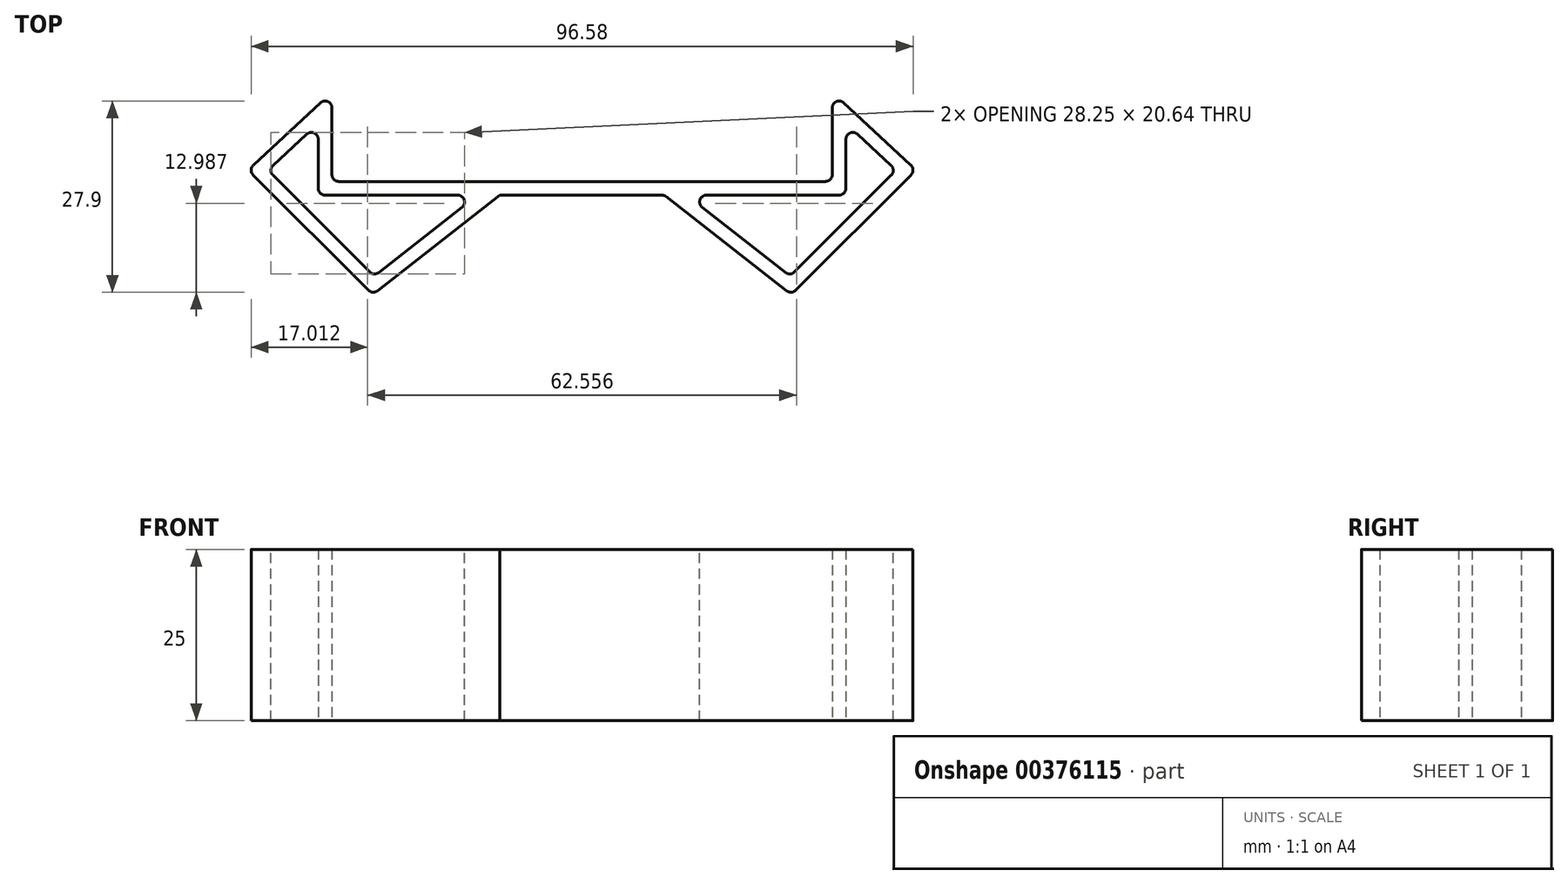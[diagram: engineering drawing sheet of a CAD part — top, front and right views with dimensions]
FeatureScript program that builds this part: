
annotation { "Feature Type Name" : "Feature", "Feature Type Description" : "" }
export const myFeature = defineFeature(function(context is Context, id is Id, definition is map)
    precondition{}
    {
        {
            var Q0;
            Q0=qCreatedBy(makeId("Top.planeOp"),FACE);
            var sketch = newSketch(context, id + "F0", { "sketchPlane" : qUnion([Q0])});
            skLineSegment(sketch, "E0", {"start": v(0, 0) * mm, "end": v(-36.5, 0) * mm});
            skLineSegment(sketch, "E1", {"start": v(-36.5, 0) * mm, "end": v(-36.5, 13.03) * mm});
            skLineSegment(sketch, "E2", {"start": v(-30.55, -16.5) * mm, "end": v(-12, -2) * mm});
            skLineSegment(sketch, "E3", {"start": v(-12, -2) * mm, "end": v(0, -2) * mm});
            skLineSegment(sketch, "E4", {"start": v(0, 14.81) * mm, "end": v(0, -16.78) * mm});
            skLineSegment(sketch, "E5.0", {"start": v(-38.5, -2) * mm, "end": v(-38.5, 15.49) * mm});
            skLineSegment(sketch, "E5.1", {"start": v(0, -2) * mm, "end": v(-38.5, -2) * mm});
            skLineSegment(sketch, "E6.0", {"start": v(-30.39, -13.83) * mm, "end": v(-15.25, -2) * mm});
            skLineSegment(sketch, "E7", {"start": v(-30.55, -16.5) * mm, "end": v(-48.73, 1.69) * mm});
            skLineSegment(sketch, "E8", {"start": v(-48.73, 1.69) * mm, "end": v(-36.5, 13.03) * mm});
            skLineSegment(sketch, "E9", {"start": v(-30.39, -13.83) * mm, "end": v(-47.26, 3.05) * mm});
            skLineSegment(sketch, "E10", {"start": v(-47.31, 0.27) * mm, "end": v(-33.52, 13.06) * mm});
            skLineSegment(sketch, "E11.MirrorCS", {"start": v(0, 0) * mm, "end": v(36.5, 0) * mm});
            skLineSegment(sketch, "E12.MirrorCS", {"start": v(0, -2) * mm, "end": v(38.5, -2) * mm});
            skLineSegment(sketch, "E13.MirrorCS", {"start": v(30.39, -13.83) * mm, "end": v(15.25, -2) * mm});
            skLineSegment(sketch, "E14.MirrorCS", {"start": v(30.55, -16.5) * mm, "end": v(12, -2) * mm});
            skLineSegment(sketch, "E15.MirrorCS", {"start": v(30.39, -13.83) * mm, "end": v(47.26, 3.05) * mm});
            skLineSegment(sketch, "E16.MirrorCS", {"start": v(30.55, -16.5) * mm, "end": v(48.73, 1.69) * mm});
            skLineSegment(sketch, "E17.MirrorCS", {"start": v(48.73, 1.69) * mm, "end": v(36.5, 13.03) * mm});
            skLineSegment(sketch, "E18.MirrorCS", {"start": v(47.31, 0.27) * mm, "end": v(33.52, 13.06) * mm});
            skLineSegment(sketch, "E19.MirrorCS", {"start": v(38.5, -2) * mm, "end": v(38.5, 15.49) * mm});
            skLineSegment(sketch, "E20.MirrorCS", {"start": v(36.5, 0) * mm, "end": v(36.5, 13.03) * mm});
            skSolve(sketch);
        }
        {
            var Q0;
            {var subQ6=sQuery(id+"F0.wireOp",EDGE,"uVpcPJW8-R3dv-cmO5-PiUA-MTJ29K8KnatB");Q0=makeQuery(id+"F0.imprint","IMPRINT",FACE,{"disambiguationData":[TD([[makeQuery(id+"F0.imprint","IMPRINT",EDGE,{"derivedFrom":subQ6}),1.0]])]});}
            var Q1;
            {var subQ0=sQuery(id+"F0.wireOp",EDGE,"s7JyDZzx-UgEq-0kRx-xTIR-yEijjmGhZAwF");var subQ1=sQuery(id+"F0.wireOp",EDGE,"E1");var subQ2=makeQuery(id+"F0.imprint","INTERSECT",VERTEX,{"derivedFrom":[subQ1,subQ0]});Q1=makeQuery(id+"F0.imprint","IMPRINT",FACE,{"disambiguationData":[TD([[makeQuery(id+"F0.imprint","IMPRINT",EDGE,{"disambiguationData":[TD([[subQ2,1.0]])],"derivedFrom":subQ1}),1.0]])]});}
            var Q2;
            {var subQ1=sQuery(id+"F0.wireOp",EDGE,"E0");Q2=makeQuery(id+"F0.imprint","IMPRINT",FACE,{"disambiguationData":[TD([[makeQuery(id+"F0.imprint","IMPRINT",EDGE,{"derivedFrom":subQ1}),1.0]])]});}
            var Q3;
            {var subQ0=sQuery(id+"F0.wireOp",EDGE,"16f77f33-1f45-4862-819a-b43949d90e552.MirrorCS");Q3=makeQuery(id+"F0.imprint","IMPRINT",FACE,{"disambiguationData":[TD([[makeQuery(id+"F0.imprint","IMPRINT",EDGE,{"derivedFrom":subQ0}),-1.0]])]});}
            var Q4;
            {var subQ7=sQuery(id+"F0.wireOp",EDGE,"e3aeeb39-8ff5-454c-905d-5596048806930.MirrorCS");Q4=makeQuery(id+"F0.imprint","IMPRINT",FACE,{"disambiguationData":[TD([[makeQuery(id+"F0.imprint","IMPRINT",EDGE,{"derivedFrom":subQ7}),-1.0]])]});}
            var Q5;
            {var subQ0=sQuery(id+"F0.wireOp",EDGE,"16f77f33-1f45-4862-819a-b43949d90e551.MirrorCS");var subQ1=sQuery(id+"F0.wireOp",EDGE,"16f77f33-1f45-4862-819a-b43949d90e550.MirrorCS");var subQ2=makeQuery(id+"F0.imprint","INTERSECT",VERTEX,{"derivedFrom":[subQ1,subQ0]});Q5=makeQuery(id+"F0.imprint","IMPRINT",FACE,{"disambiguationData":[TD([[makeQuery(id+"F0.imprint","IMPRINT",EDGE,{"disambiguationData":[TD([[subQ2,1.0]])],"derivedFrom":subQ1}),-1.0]])]});}
            var Q6;
            {var subQ0=sQuery(id+"F0.wireOp",EDGE,"E8");var subQ1=sQuery(id+"F0.wireOp",EDGE,"E5.0");var subQ2=makeQuery(id+"F0.imprint","INTERSECT",VERTEX,{"derivedFrom":[subQ1,subQ0]});Q6=makeQuery(id+"F0.imprint","IMPRINT",FACE,{"disambiguationData":[TD([[makeQuery(id+"F0.imprint","IMPRINT",EDGE,{"disambiguationData":[TD([[subQ2,1.0]])],"derivedFrom":subQ1}),1.0]])]});}
            var Q7;
            {var subQ0=sQuery(id+"F0.wireOp",EDGE,"E8");var subQ1=sQuery(id+"F0.wireOp",EDGE,"E7");var subQ2=makeQuery(id+"F0.imprint","INTERSECT",VERTEX,{"derivedFrom":[subQ1,subQ0]});Q7=makeQuery(id+"F0.imprint","IMPRINT",FACE,{"disambiguationData":[TD([[makeQuery(id+"F0.imprint","IMPRINT",EDGE,{"disambiguationData":[TD([[subQ2,1.0]])],"derivedFrom":subQ1}),-1.0]])]});}
            var Q8;
            {var subQ1=sQuery(id+"F0.wireOp",EDGE,"E2");Q8=makeQuery(id+"F0.imprint","IMPRINT",FACE,{"disambiguationData":[TD([[makeQuery(id+"F0.imprint","IMPRINT",EDGE,{"derivedFrom":subQ1}),1.0]])]});}
            var Q9;
            {var subQ5=sQuery(id+"F0.wireOp",EDGE,"E11.MirrorCS");Q9=makeQuery(id+"F0.imprint","IMPRINT",FACE,{"disambiguationData":[TD([[makeQuery(id+"F0.imprint","IMPRINT",EDGE,{"derivedFrom":subQ5}),-1.0]])]});}
            var Q10;
            {var subQ0=sQuery(id+"F0.wireOp",EDGE,"E17.MirrorCS");var subQ1=sQuery(id+"F0.wireOp",EDGE,"E15.MirrorCS");var subQ2=makeQuery(id+"F0.imprint","INTERSECT",VERTEX,{"derivedFrom":[subQ1,subQ0]});Q10=makeQuery(id+"F0.imprint","IMPRINT",FACE,{"disambiguationData":[TD([[makeQuery(id+"F0.imprint","IMPRINT",EDGE,{"disambiguationData":[TD([[subQ2,1.0]])],"derivedFrom":subQ1}),1.0]])]});}
            var Q11;
            {var subQ0=sQuery(id+"F0.wireOp",EDGE,"E17.MirrorCS");var subQ1=sQuery(id+"F0.wireOp",EDGE,"E15.MirrorCS");var subQ2=makeQuery(id+"F0.imprint","INTERSECT",VERTEX,{"derivedFrom":[subQ1,subQ0]});Q11=makeQuery(id+"F0.imprint","IMPRINT",FACE,{"disambiguationData":[TD([[makeQuery(id+"F0.imprint","IMPRINT",EDGE,{"disambiguationData":[TD([[subQ2,1.0]])],"derivedFrom":subQ1}),-1.0]])]});}
            var Q12;
            {var subQ0=sQuery(id+"F0.wireOp",EDGE,"E20.MirrorCS");var subQ1=sQuery(id+"F0.wireOp",EDGE,"E17.MirrorCS");var subQ2=makeQuery(id+"F0.imprint","INTERSECT",VERTEX,{"derivedFrom":[subQ1,subQ0]});Q12=makeQuery(id+"F0.imprint","IMPRINT",FACE,{"disambiguationData":[TD([[makeQuery(id+"F0.imprint","IMPRINT",EDGE,{"disambiguationData":[TD([[subQ2,1.0]])],"derivedFrom":subQ1}),1.0]])]});}
            var Q13;
            {var subQ1=sQuery(id+"F0.wireOp",EDGE,"E13.MirrorCS");Q13=makeQuery(id+"F0.imprint","IMPRINT",FACE,{"disambiguationData":[TD([[makeQuery(id+"F0.imprint","IMPRINT",EDGE,{"derivedFrom":subQ1}),1.0]])]});}
            extrude(context, id + "F1", {"entities" : qUnion([Q0, Q1, Q2, Q3, Q4, Q5, Q6, Q7, Q8, Q9, Q10, Q11, Q12, Q13]), "depth" : 25 * mm});
        }
        {
            var Q0;
            Q0=makeQuery(id+"F1.opExtrude","SWEPT_EDGE",EDGE,{"disambiguationData":[OSD([sQuery(id+"F0.wireOp",EDGE,"E1"),sQuery(id+"F0.wireOp",EDGE,"s7JyDZzx-UgEq-0kRx-xTIR-yEijjmGhZAwF")])]});
            var Q1;
            Q1=makeQuery(id+"F1.opExtrude","SWEPT_EDGE",EDGE,{"disambiguationData":[OSD([sQuery(id+"F0.wireOp",EDGE,"s7JyDZzx-UgEq-0kRx-xTIR-yEijjmGhZAwF"),sQuery(id+"F0.wireOp",EDGE,"uVpcPJW8-R3dv-cmO5-PiUA-MTJ29K8KnatB")])]});
            var Q2;
            Q2=makeQuery(id+"F1.opExtrude","SWEPT_EDGE",EDGE,{"disambiguationData":[OSD([sQuery(id+"F0.wireOp",EDGE,"uVpcPJW8-R3dv-cmO5-PiUA-MTJ29K8KnatB"),sQuery(id+"F0.wireOp",EDGE,"E2")])]});
            var Q3;
            Q3=makeQuery(id+"F1.opExtrude","SWEPT_EDGE",EDGE,{"disambiguationData":[OSD([sQuery(id+"F0.wireOp",EDGE,"E0"),sQuery(id+"F0.wireOp",EDGE,"E1")])]});
            var Q4;
            Q4=makeQuery(id+"F1.opExtrude","SWEPT_EDGE",EDGE,{"disambiguationData":[OSD([sQuery(id+"F0.wireOp",EDGE,"E5.0"),sQuery(id+"F0.wireOp",EDGE,"E5.1")])]});
            var Q5;
            Q5=makeQuery(id+"F1.opExtrude","SWEPT_EDGE",EDGE,{"disambiguationData":[OSD([sQuery(id+"F0.wireOp",EDGE,"16f77f33-1f45-4862-819a-b43949d90e550.MirrorCS"),sQuery(id+"F0.wireOp",EDGE,"e3aeeb39-8ff5-454c-905d-5596048806930.MirrorCS")])]});
            var Q6;
            Q6=makeQuery(id+"F1.opExtrude","SWEPT_EDGE",EDGE,{"disambiguationData":[OSD([sQuery(id+"F0.wireOp",EDGE,"16f77f33-1f45-4862-819a-b43949d90e550.MirrorCS"),sQuery(id+"F0.wireOp",EDGE,"16f77f33-1f45-4862-819a-b43949d90e551.MirrorCS")])]});
            var Q7;
            Q7=makeQuery(id+"F1.opExtrude","SWEPT_EDGE",EDGE,{"disambiguationData":[OSD([sQuery(id+"F0.wireOp",EDGE,"16f77f33-1f45-4862-819a-b43949d90e551.MirrorCS"),sQuery(id+"F0.wireOp",EDGE,"16f77f33-1f45-4862-819a-b43949d90e552.MirrorCS")])]});
            var Q8;
            Q8=makeQuery(id+"F1.opExtrude","SWEPT_EDGE",EDGE,{"disambiguationData":[OSD([sQuery(id+"F0.wireOp",EDGE,"16f77f33-1f45-4862-819a-b43949d90e555.MirrorCS"),sQuery(id+"F0.wireOp",EDGE,"6a9659e7-4544-4aa1-b53f-422f2103a2140.MirrorCS")])]});
            var Q9;
            Q9=makeQuery(id+"F1.opExtrude","SWEPT_EDGE",EDGE,{"disambiguationData":[OSD([sQuery(id+"F0.wireOp",EDGE,"16f77f33-1f45-4862-819a-b43949d90e552.MirrorCS"),sQuery(id+"F0.wireOp",EDGE,"16f77f33-1f45-4862-819a-b43949d90e553.MirrorCS")])]});
            var Q10;
            Q10=makeQuery(id+"F1.opExtrude","SWEPT_EDGE",EDGE,{"disambiguationData":[OSD([sQuery(id+"F0.wireOp",EDGE,"16f77f33-1f45-4862-819a-b43949d90e554.MirrorCS"),sQuery(id+"F0.wireOp",EDGE,"16f77f33-1f45-4862-819a-b43949d90e557.MirrorCS")])]});
            var Q11;
            Q11=makeQuery(id+"F1.opExtrude","SWEPT_EDGE",EDGE,{"disambiguationData":[OSD([sQuery(id+"F0.wireOp",EDGE,"16f77f33-1f45-4862-819a-b43949d90e554.MirrorCS"),sQuery(id+"F0.wireOp",EDGE,"6a9659e7-4544-4aa1-b53f-422f2103a2140.MirrorCS")])]});
            var Q12;
            Q12=makeQuery(id+"F1.opExtrude","SWEPT_EDGE",EDGE,{"disambiguationData":[OSD([sQuery(id+"F0.wireOp",EDGE,"16f77f33-1f45-4862-819a-b43949d90e555.MirrorCS"),sQuery(id+"F0.wireOp",EDGE,"16f77f33-1f45-4862-819a-b43949d90e556.MirrorCS")])]});
            var Q13;
            Q13=makeQuery(id+"F1.opExtrude","SWEPT_EDGE",EDGE,{"disambiguationData":[OSD([sQuery(id+"F0.wireOp",EDGE,"16f77f33-1f45-4862-819a-b43949d90e556.MirrorCS"),sQuery(id+"F0.wireOp",EDGE,"16f77f33-1f45-4862-819a-b43949d90e557.MirrorCS")])]});
            var Q14;
            Q14=makeQuery(id+"F1.opExtrude","SWEPT_EDGE",EDGE,{"disambiguationData":[OSD([sQuery(id+"F0.wireOp",EDGE,"12d51f8c-d412-4ac5-94a4-2e461e6358c8.0"),sQuery(id+"F0.wireOp",EDGE,"12d51f8c-d412-4ac5-94a4-2e461e6358c8.1")])]});
            var Q15;
            Q15=makeQuery(id+"F1.opExtrude","SWEPT_EDGE",EDGE,{"disambiguationData":[OSD([sQuery(id+"F0.wireOp",EDGE,"12d51f8c-d412-4ac5-94a4-2e461e6358c8.1"),sQuery(id+"F0.wireOp",EDGE,"E5.0")])]});
            var Q16;
            Q16=makeQuery(id+"F1.opExtrude","SWEPT_EDGE",EDGE,{"disambiguationData":[OSD([sQuery(id+"F0.wireOp",EDGE,"12d51f8c-d412-4ac5-94a4-2e461e6358c8.0"),sQuery(id+"F0.wireOp",EDGE,"E6.0")])]});
            var Q17;
            Q17=makeQuery(id+"F1.opExtrude","SWEPT_EDGE",EDGE,{"disambiguationData":[OSD([sQuery(id+"F0.wireOp",EDGE,"E5.1"),sQuery(id+"F0.wireOp",EDGE,"E6.0")])]});
            var Q18;
            Q18=makeQuery(id+"F1.opExtrude","SWEPT_EDGE",EDGE,{"disambiguationData":[OSD([sQuery(id+"F0.wireOp",EDGE,"E12.MirrorCS"),sQuery(id+"F0.wireOp",EDGE,"E13.MirrorCS")])]});
            var Q19;
            Q19=makeQuery(id+"F1.opExtrude","SWEPT_EDGE",EDGE,{"disambiguationData":[OSD([sQuery(id+"F0.wireOp",EDGE,"E13.MirrorCS"),sQuery(id+"F0.wireOp",EDGE,"E15.MirrorCS")])]});
            var Q20;
            Q20=makeQuery(id+"F1.opExtrude","SWEPT_EDGE",EDGE,{"disambiguationData":[OSD([sQuery(id+"F0.wireOp",EDGE,"E12.MirrorCS"),sQuery(id+"F0.wireOp",EDGE,"E19.MirrorCS")])]});
            var Q21;
            Q21=makeQuery(id+"F1.opExtrude","SWEPT_EDGE",EDGE,{"disambiguationData":[OSD([sQuery(id+"F0.wireOp",EDGE,"E18.MirrorCS"),sQuery(id+"F0.wireOp",EDGE,"E19.MirrorCS")])]});
            var Q22;
            Q22=makeQuery(id+"F1.opExtrude","SWEPT_EDGE",EDGE,{"disambiguationData":[OSD([sQuery(id+"F0.wireOp",EDGE,"E15.MirrorCS"),sQuery(id+"F0.wireOp",EDGE,"E18.MirrorCS")])]});
            var Q23;
            Q23=makeQuery(id+"F1.opExtrude","SWEPT_EDGE",EDGE,{"disambiguationData":[OSD([sQuery(id+"F0.wireOp",EDGE,"E12.MirrorCS"),sQuery(id+"F0.wireOp",EDGE,"E14.MirrorCS")])]});
            var Q24;
            Q24=makeQuery(id+"F1.opExtrude","SWEPT_EDGE",EDGE,{"disambiguationData":[OSD([sQuery(id+"F0.wireOp",EDGE,"E14.MirrorCS"),sQuery(id+"F0.wireOp",EDGE,"E16.MirrorCS")])]});
            var Q25;
            Q25=makeQuery(id+"F1.opExtrude","SWEPT_EDGE",EDGE,{"disambiguationData":[OSD([sQuery(id+"F0.wireOp",EDGE,"E17.MirrorCS"),sQuery(id+"F0.wireOp",EDGE,"E20.MirrorCS")])]});
            var Q26;
            Q26=makeQuery(id+"F1.opExtrude","SWEPT_EDGE",EDGE,{"disambiguationData":[OSD([sQuery(id+"F0.wireOp",EDGE,"E11.MirrorCS"),sQuery(id+"F0.wireOp",EDGE,"E20.MirrorCS")])]});
            var Q27;
            Q27=makeQuery(id+"F1.opExtrude","SWEPT_EDGE",EDGE,{"disambiguationData":[OSD([sQuery(id+"F0.wireOp",EDGE,"E16.MirrorCS"),sQuery(id+"F0.wireOp",EDGE,"E17.MirrorCS")])]});
            var Q28;
            Q28=makeQuery(id+"F1.opExtrude","SWEPT_EDGE",EDGE,{"disambiguationData":[OSD([sQuery(id+"F0.wireOp",EDGE,"E9"),sQuery(id+"F0.wireOp",EDGE,"E10")])]});
            var Q29;
            Q29=makeQuery(id+"F1.opExtrude","SWEPT_EDGE",EDGE,{"disambiguationData":[OSD([sQuery(id+"F0.wireOp",EDGE,"E7"),sQuery(id+"F0.wireOp",EDGE,"E8")])]});
            fillet(context, id + "F2", {"entities" : qUnion([Q0, Q1, Q2, Q3, Q4, Q5, Q6, Q7, Q8, Q9, Q10, Q11, Q12, Q13, Q14, Q15, Q16, Q17, Q18, Q19, Q20, Q21, Q22, Q23, Q24, Q25, Q26, Q27, Q28, Q29]), "radius" : 1 * mm, "tangentPropagation" : true, "allowEdgeOverflow" : false});
        }
    });
